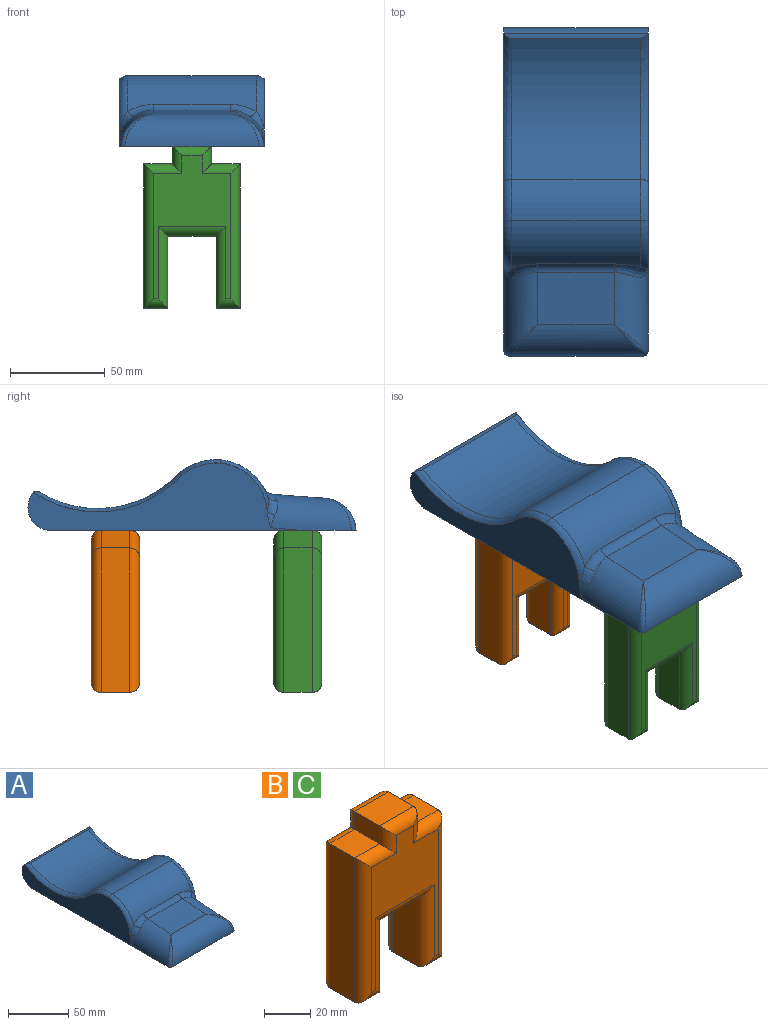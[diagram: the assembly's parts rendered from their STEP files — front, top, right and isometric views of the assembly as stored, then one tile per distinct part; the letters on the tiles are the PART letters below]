
ASSEMBLY  parts=3 mates=2
PART A: 38 faces, bbox 79.9x175.7x54.4 mm
  f0: plane 143.3x35.45mm, normal (-1,0,0), area 2574.6mm2, adj f2,f7,f10,f13,f16,f20,f30
  f1: plane 143.3x35.45mm, normal (1,0,0), area 2574.6mm2, adj f2,f7,f8,f11,f12,f17,f25
  f2: plane 163.18x76.43mm, normal (0,0,-1), area 12412mm2, adj f0,f1,f7,f8,f9,f10,f36,f37
  f3: cylinder r=779.43mm len=40.64mm, axis (1,0,0), area 1112.1mm2, adj f8,f9,f10,f28
  f4: cylinder r=29.22mm len=67.8mm, axis (1,0,0), area 2004mm2, adj f5,f24,f27,f28,f29,f32
  f5: cylinder r=30.71mm len=67.8mm, axis (1,0,0), area 1563.2mm2, adj f4,f15,f23,f33
  f6: cylinder r=58.84mm len=74.44mm, axis (1,0,0), area 5520.3mm2, adj f15,f19,f21,f35
  f7: cylinder r=12.12mm len=76.2mm, axis (1,0,0), area 1994.2mm2, adj f0,f1,f2,f17,f19,f20,f21,f35
  f8: torus R=797.21mm, axis (1,0,0), area 918.8mm2, adj f1,f2,f3,f25,f26,f27,f36
  f9: cylinder r=17.78mm len=70.99mm, axis (1,0,0), area 1456mm2, adj f2,f3,f36,f37
  f10: torus R=797.21mm, axis (1,0,0), area 918.8mm2, adj f0,f2,f3,f29,f30,f31,f37
  f11: cone r=27.44mm half-angle=45deg, axis (-1,0,0), area 3.7mm2, adj f1,f12,f24,f25
  f12: cone r=28.93mm half-angle=45deg, axis (-1,0,0), area 2.1mm2, adj f1,f11,f14,f23
  f13: cone r=29.22mm half-angle=45deg, axis (1,0,0), area 3.7mm2, adj f0,f16,f30,f32
  f14: plane 0.07x0.05mm, normal (0.71,0.48,0.52), area 0mm2, adj f12,f17,f21,f22,f23
  f15: plane 67.81x0.18mm, normal (0,0.68,0.73), area 16.8mm2, adj f5,f6,f21,f22,f23,f33,f34,f35
  f16: cone r=30.71mm half-angle=45deg, axis (1,0,0), area 2.1mm2, adj f0,f13,f18,f33
  f17: cone r=58.84mm half-angle=45deg, axis (1,0,0), area 8.1mm2, adj f1,f7,f14,f21
  f18: plane 0.07x0.05mm, normal (-0.71,0.48,0.52), area 0mm2, adj f16,f20,f33,f34,f35
  f19: plane 75.59x2.26mm, normal (0,0.13,0.99), area 166.5mm2, adj f6,f7,f21,f35
  f20: cone r=60.62mm half-angle=45deg, axis (-1,0,0), area 8.1mm2, adj f0,f7,f18,f35
  f21: torus R=64.68mm, axis (-1,0,0), area 380.4mm2, adj f6,f7,f14,f15,f17,f19,f22
  f22: cylinder r=5.84mm len=4.13mm, axis (0,0.73,-0.68), area 0.7mm2, adj f14,f15,f21,f23
  f23: torus R=24.87mm, axis (1,0,0), area 103.8mm2, adj f5,f12,f14,f15,f22,f24
  f24: torus R=23.38mm, axis (1,0,0), area 166.8mm2, adj f4,f11,f23,f26
  f25: bspline ~9.84x6.73mm, area 17mm2, adj f1,f8,f11,f26
  f26: bspline ~11.96x8.41mm, area 56.4mm2, adj f8,f24,f25,f27
  f27: bspline ~17.94x8.03mm, area 78mm2, adj f4,f8,f26,f28
  f28: cylinder r=5.84mm len=40.64mm, axis (1,0,0), area 232.2mm2, adj f3,f4,f27,f29
  f29: bspline ~17.94x8.03mm, area 78mm2, adj f4,f10,f28,f31
  f30: bspline ~9.83x6.74mm, area 17mm2, adj f0,f10,f13,f31
  f31: bspline ~12.45x8.39mm, area 56.4mm2, adj f10,f29,f30,f32
  f32: torus R=23.38mm, axis (-1,0,0), area 166.8mm2, adj f4,f13,f31,f33
  f33: torus R=24.87mm, axis (-1,0,0), area 103.8mm2, adj f5,f15,f16,f18,f32,f34
  f34: cylinder r=5.84mm len=4.13mm, axis (0,0.73,-0.68), area 0.7mm2, adj f15,f18,f33,f35
  f35: torus R=64.68mm, axis (1,0,0), area 380.4mm2, adj f6,f7,f15,f18,f19,f20,f34
  f36: bspline ~18.04x17.79mm, area 47.5mm2, adj f2,f8,f9
  f37: bspline ~18.04x17.79mm, area 47.2mm2, adj f2,f9,f10
PART B: 38 faces, bbox 50.8x25.4x85.6 mm
  f0: plane 15.24x9.38mm, normal (-1,0,0), area 142.9mm2, adj f1,f11,f19,f31
  f1: plane 15.24x15mm, normal (0,0,1), area 228.6mm2, adj f0,f2,f17,f29
  f2: plane 76.2x15.24mm, normal (-1,0,0), area 1161.3mm2, adj f1,f3,f15,f27
  f3: plane 15.24x12.7mm, normal (0,0,-1), area 193.5mm2, adj f2,f4,f14,f26
  f4: plane 38.1x15.24mm, normal (1,0,0), area 580.6mm2, adj f3,f5,f16,f28
  f5: plane 25.4x15.24mm, normal (0,0,-1), area 387.1mm2, adj f4,f6,f18,f30
  f6: plane 38.1x15.24mm, normal (-1,0,0), area 580.6mm2, adj f5,f7,f20,f32
  f7: plane 15.24x12.7mm, normal (0,0,-1), area 193.5mm2, adj f6,f8,f22,f34
  f8: plane 76.2x15.24mm, normal (1,0,0), area 1161.3mm2, adj f7,f9,f24,f36
  f9: plane 15.24x15mm, normal (0,0,1), area 228.6mm2, adj f8,f10,f25,f37
  f10: plane 15.24x9.38mm, normal (1,0,0), area 142.9mm2, adj f9,f11,f23,f35
  f11: plane 20.8x15.24mm, normal (0,0,1), area 316.9mm2, adj f0,f10,f21,f33
  f12: plane 75.42x40.64mm, normal (0,-1,0), area 1428.8mm2, adj f26,f27,f28,f29,f30,f31,f32,f33
  f13: plane 75.42x40.64mm, normal (0,1,0), area 1428.8mm2, adj f14,f15,f16,f17,f18,f19,f20,f21
  f14: cylinder r=5.08mm len=12.7mm, axis (1,0,0), area 71.9mm2, adj f3,f13,f15,f16
  f15: cylinder r=5.08mm len=76.2mm, axis (0,0,-1), area 578.6mm2, adj f2,f13,f14,f17
  f16: cylinder r=5.08mm len=43.18mm, axis (0,0,1), area 304mm2, adj f4,f13,f14,f18
  f17: cylinder r=5.08mm len=20.08mm, axis (-1,0,0), area 119.7mm2, adj f1,f13,f15,f19
  f18: cylinder r=5.08mm len=35.56mm, axis (1,0,0), area 232.1mm2, adj f5,f13,f16,f20
  f19: cylinder r=5.08mm len=14.46mm, axis (0,0,-1), area 74.8mm2, adj f0,f13,f17,f21
  f20: cylinder r=5.08mm len=43.18mm, axis (0,0,-1), area 304mm2, adj f6,f13,f18,f22
  f21: cylinder r=5.08mm len=20.8mm, axis (-1,0,0), area 136.5mm2, adj f11,f13,f19,f23
  f22: cylinder r=5.08mm len=12.7mm, axis (1,0,0), area 71.9mm2, adj f7,f13,f20,f24
  f23: cylinder r=5.08mm len=14.46mm, axis (0,0,1), area 74.8mm2, adj f10,f13,f21,f25
  f24: cylinder r=5.08mm len=76.2mm, axis (0,0,1), area 578.6mm2, adj f8,f13,f22,f25
  f25: cylinder r=5.08mm len=20.08mm, axis (-1,0,0), area 119.7mm2, adj f9,f13,f23,f24
  f26: cylinder r=5.08mm len=12.7mm, axis (-1,0,0), area 71.9mm2, adj f3,f12,f27,f28
  f27: cylinder r=5.08mm len=76.2mm, axis (0,0,1), area 578.6mm2, adj f2,f12,f26,f29
  f28: cylinder r=5.08mm len=43.18mm, axis (0,0,-1), area 304mm2, adj f4,f12,f26,f30
  f29: cylinder r=5.08mm len=20.08mm, axis (1,0,0), area 119.7mm2, adj f1,f12,f27,f31
  f30: cylinder r=5.08mm len=35.56mm, axis (-1,0,0), area 232.1mm2, adj f5,f12,f28,f32
  f31: cylinder r=5.08mm len=14.46mm, axis (0,0,1), area 74.8mm2, adj f0,f12,f29,f33
  f32: cylinder r=5.08mm len=43.18mm, axis (0,0,1), area 304mm2, adj f6,f12,f30,f34
  f33: cylinder r=5.08mm len=20.8mm, axis (1,0,0), area 136.5mm2, adj f11,f12,f31,f35
  f34: cylinder r=5.08mm len=12.7mm, axis (-1,0,0), area 71.9mm2, adj f7,f12,f32,f36
  f35: cylinder r=5.08mm len=14.46mm, axis (0,0,-1), area 74.8mm2, adj f10,f12,f33,f37
  f36: cylinder r=5.08mm len=76.2mm, axis (0,0,-1), area 578.6mm2, adj f8,f12,f34,f37
  f37: cylinder r=5.08mm len=20.08mm, axis (1,0,0), area 119.7mm2, adj f9,f12,f35,f36
PART C: same geometry as B
PLACE A t=(33.53,-55.61,3.9)mm fixed
PLACE B t=(67.69,-93.71,-54.79)mm
PLACE C t=(67.69,-190.01,-54.79)mm
MATE fastened A.f2 <-> B.f11  axis (0,0,-1) through (41.99,-233.41,-12.47)mm
MATE fastened C.f11 <-> A.f2  axis (0,0,1) through (41.99,-202.71,-12.47)mm
